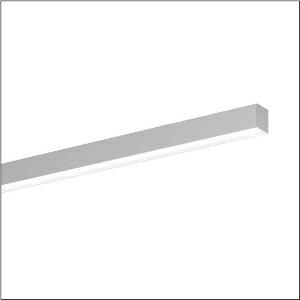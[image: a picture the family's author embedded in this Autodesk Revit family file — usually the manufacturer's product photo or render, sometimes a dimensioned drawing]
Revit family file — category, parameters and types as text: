
# Revit family: silica_r__21_51mx20db42sb_cda5
name_source: partatom
category: Lighting Fixtures
units: mm (PartAtom-declared; Revit-internal decimal feet)

## family parameters
Cut with Voids When Loaded = No
Host = Face
Light Source = No
Part Type = Normal
Room Calculation Point = No
Round Connector Dimension = Use Diameter
Shared = No

## types (1)
- --- (1 x LED, 3000 lm, 19 W, 4000K)
    Apparent Load = 19 VA
    CIE Flux Codes = 48 79 96 100 100
    Color Rendering = 80
    Color Temperature = 4000K
    Default Elevation = 1800 mm
    Description = Silica® 21, office luminaire, primary optical cover: cover, of PMMA, opal, light emission: direct distribution, primary light characteristic: symmetric, installation type: surface-mounted, LED, rated luminous flux: 3.000lm, luminous efficacy: 158lm/W, light colour: 840, colour temperature: 4000K, with terminal, 3+2-pole, max. 2.5mm², mains connection: 220..240V, AC, 50/60Hz, rated input power: 19W, luminaire housing, of aluminium, metallic grey (RAL 9006), length: 1.504mm, width: 53mm, height: 53mm, protection rating (complete): IP20, insulation class (complete): insulation class I (protective earthing), certification: CE, permissible operating ambient temperature: 0..+35°C, standard: EN 50419, packaging unit: 1 piece
    Height = 0 mm  [stored 0 ft]
    Lamp = 1 x LED
    Lamp Light Flux = 3000 lm
    Lamp Power = 19 W
    Lamp count = 1
    Length = 1504 mm
    Luminous efficacy = 158 lm/W
    Manufacturer = Siteco
    ModVariant = No
    Model = 51MX20DB42SB
    Mounting Place = Ceiling
    Mounting Type = Recessed
    Number of Poles = 1
    OnlyDefault = Yes
    Power Factor = 1
    Product Name = Silica® 21
    Product group = office luminaire | ceiling recessed
    ProductGroupID = 400
    Protection Class = Protection class I
    Protection Degree = IP 20
    RLX_Detail_Level = 1
    RLX_Emergency_Light_Flux = 0 lm
    RLX_Emergency_Type = 0
    RLX_Emergency_Type_DB = No
    RlxData = <blob elided: 26273 chars, md5=6c04fb18>
    Socket = socket
    Standby Power = 0 W
    System Light Flux = 3000 lm
    System Power = 19 W
    Type Comments = factory setting: luminous flux: 100 % | dim-lin: 254 | 218 mA
    Type Image = l_1335933.jpg
    URL = http://relux.com
    VarID = @adj_086937
    Voltage = 0 V
    Weight = 0.00 kg
    Width = 53 mm

note: [stored X ft] marks values corroborated as IEEE doubles in the binary element streams (Revit-internal decimal feet)

## geometry (parser evidence)
native form markers: Blend x4, Sweep x9
no freeform markers — native parametric forms only
